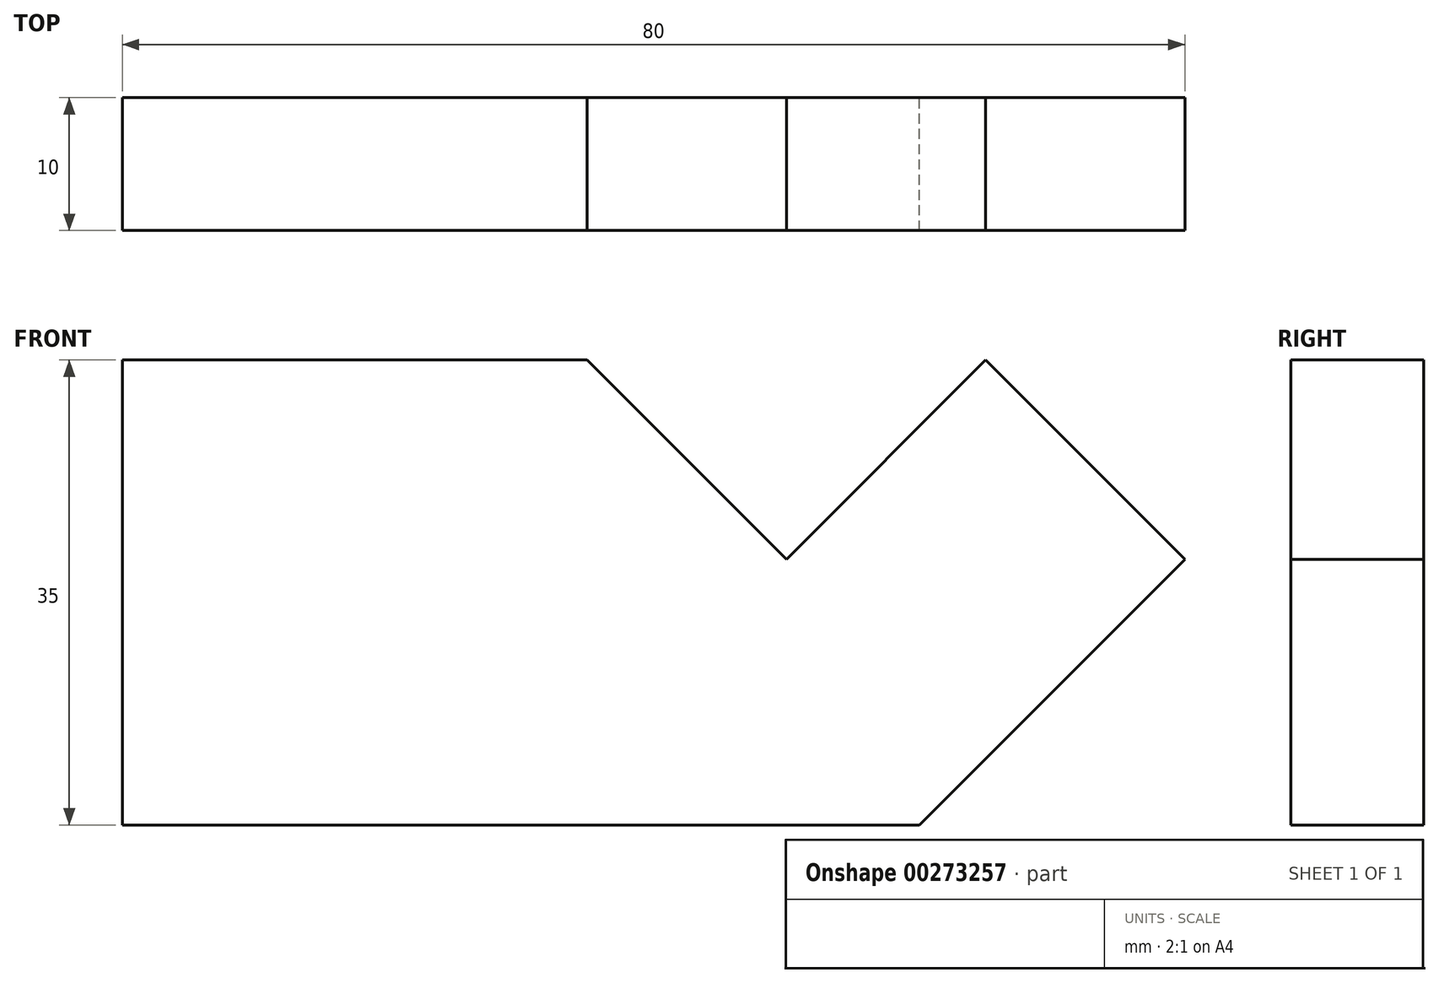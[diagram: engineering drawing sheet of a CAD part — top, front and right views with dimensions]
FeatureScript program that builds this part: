
annotation { "Feature Type Name" : "Feature", "Feature Type Description" : "" }
export const myFeature = defineFeature(function(context is Context, id is Id, definition is map)
    precondition{}
    {
        {
            var Q0;
            Q0=qCreatedBy(makeId("Front.planeOp"),FACE);
            var sketch = newSketch(context, id + "F0", { "sketchPlane" : qUnion([Q0])});
            skLineSegment(sketch, "E0", {"start": v(0, 0) * mm, "end": v(0, 35) * mm});
            skLineSegment(sketch, "E1", {"start": v(0, 35) * mm, "end": v(35, 35) * mm});
            skLineSegment(sketch, "E2", {"start": v(50, 20) * mm, "end": v(35, 35) * mm});
            skLineSegment(sketch, "E3", {"start": v(50, 20) * mm, "end": v(65, 35) * mm});
            skLineSegment(sketch, "E4", {"start": v(0, 0) * mm, "end": v(60, 0) * mm});
            skLineSegment(sketch, "E5", {"start": v(80, 20) * mm, "end": v(65, 35) * mm});
            skLineSegment(sketch, "E6", {"start": v(80, 20) * mm, "end": v(60, 0) * mm});
            skSolve(sketch);
        }
        {
            var Q0;
            Q0=makeQuery(id+"F0.imprint","IMPRINT",FACE,{"disambiguationData":[TD([[makeQuery(id+"F0.imprint","IMPRINT",EDGE,{"derivedFrom":sQuery(id+"F0.wireOp",EDGE,"E0")}),-1.0]])]});
            extrude(context, id + "F1", {"entities" : qUnion([Q0]), "depth" : 10 * mm});
        }
    });
